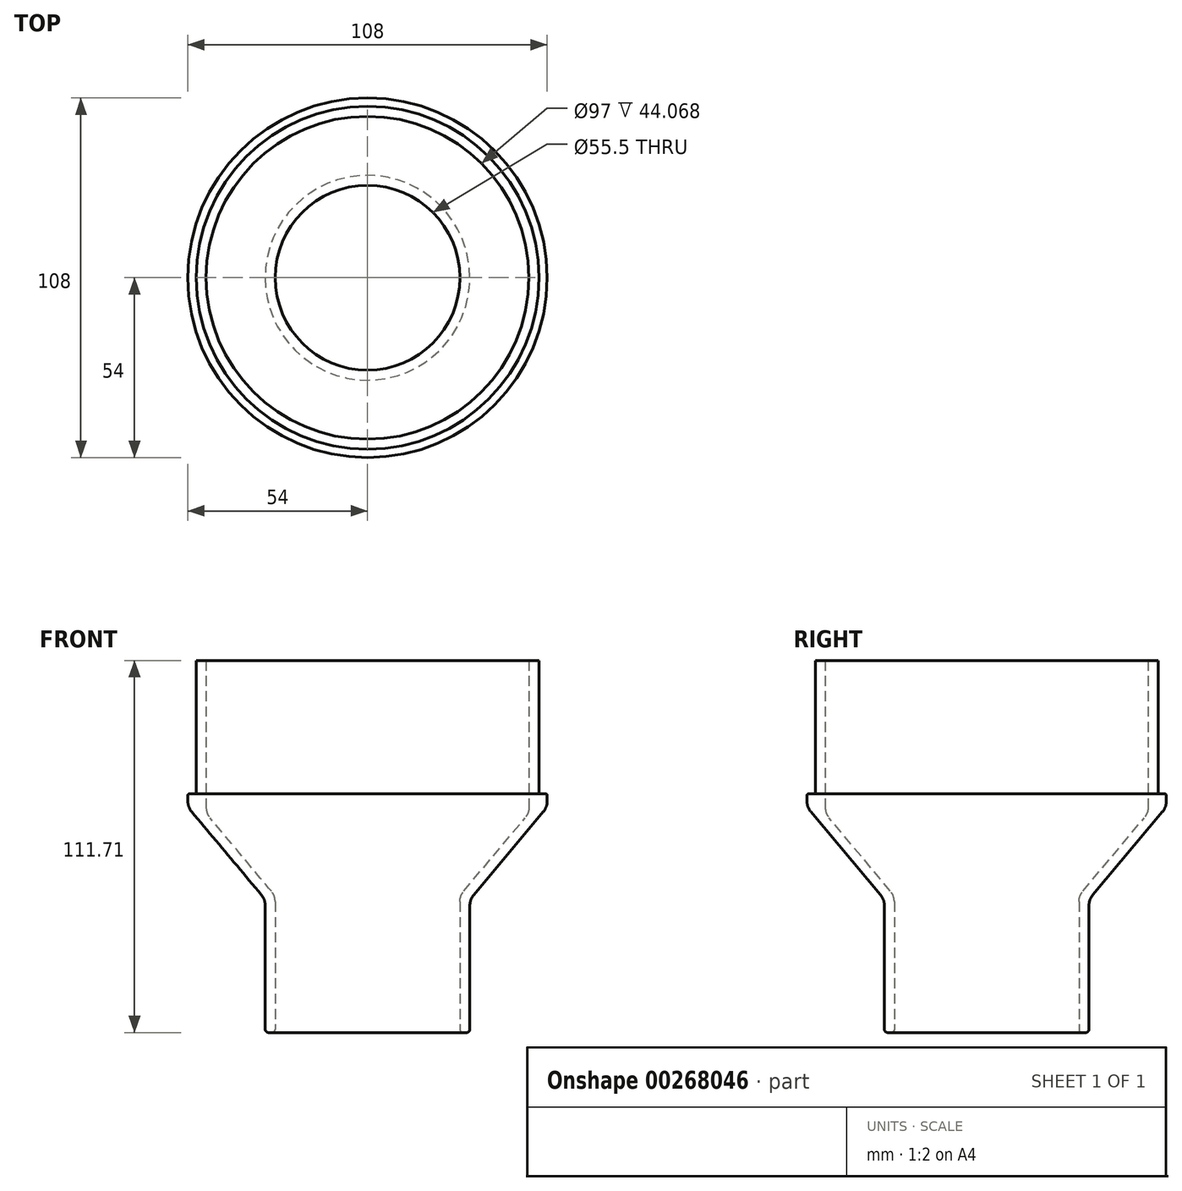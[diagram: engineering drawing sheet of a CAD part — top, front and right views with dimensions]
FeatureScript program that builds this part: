
annotation { "Feature Type Name" : "Feature", "Feature Type Description" : "" }
export const myFeature = defineFeature(function(context is Context, id is Id, definition is map)
    precondition{}
    {
        {
            var Q0;
            Q0=qCreatedBy(makeId("Front.planeOp"),FACE);
            var sketch = newSketch(context, id + "F0", { "sketchPlane" : qUnion([Q0])});
            skLineSegment(sketch, "E0", {"start": v(30.75, 0) * mm, "end": v(30.75, 38.18) * mm});
            skLineSegment(sketch, "E1", {"start": v(31.92, 41.4) * mm, "end": v(52.83, 66.31) * mm});
            skLineSegment(sketch, "E2", {"start": v(54, 69.53) * mm, "end": v(54, 71.7) * mm});
            skLineSegment(sketch, "E3", {"start": v(54, 71.7) * mm, "end": v(51.5, 71.7) * mm});
            skLineSegment(sketch, "E4", {"start": v(51.5, 71.7) * mm, "end": v(51.5, 111.7) * mm});
            skLineSegment(sketch, "E5", {"start": v(0, -37.25) * mm, "end": v(0, 130.62) * mm, "construction": true});
            skLineSegment(sketch, "E6", {"start": v(51.5, 111.7) * mm, "end": v(48.5, 111.7) * mm});
            skLineSegment(sketch, "E7", {"start": v(48.5, 111.7) * mm, "end": v(48.5, 67.64) * mm});
            skLineSegment(sketch, "E8", {"start": v(47.33, 64.43) * mm, "end": v(28.92, 42.49) * mm});
            skLineSegment(sketch, "E9", {"start": v(27.75, 39.27) * mm, "end": v(27.75, 0) * mm});
            skLineSegment(sketch, "E10", {"start": v(27.75, 0) * mm, "end": v(30.75, 0) * mm});
            skPoint(sketch, "E11.visualSharp", {"position": v(48.5, 65.82) * mm});
            skPoint(sketch, "E12.visualSharp", {"position": v(30.75, 40) * mm});
            skPoint(sketch, "E13.visualSharp", {"position": v(27.75, 41.1) * mm});
            skPoint(sketch, "E14.visualSharp", {"position": v(54, 67.7) * mm});
            skLineSegment(sketch, "E15", {"start": v(47.33, 64.43) * mm, "end": v(47.33, 64.43) * mm});
            skLineSegment(sketch, "E16", {"start": v(48.5, 67.64) * mm, "end": v(48.5, 67.64) * mm});
            skLineSegment(sketch, "E17", {"start": v(52.83, 66.31) * mm, "end": v(52.83, 66.31) * mm});
            skLineSegment(sketch, "E18", {"start": v(54, 69.53) * mm, "end": v(54, 69.53) * mm});
            skLineSegment(sketch, "E19", {"start": v(28.92, 42.49) * mm, "end": v(28.92, 42.49) * mm});
            skLineSegment(sketch, "E20", {"start": v(27.75, 39.27) * mm, "end": v(27.75, 39.27) * mm});
            skLineSegment(sketch, "E21", {"start": v(31.92, 41.4) * mm, "end": v(31.92, 41.4) * mm});
            skLineSegment(sketch, "E22", {"start": v(30.75, 38.18) * mm, "end": v(30.75, 38.18) * mm});
            skArc(sketch, "E23.filletArc", {"start": v(47.33, 64.43) * mm, "mid": v(48.2, 65.93) * mm, "end": v(48.5, 67.64) * mm});
            skArc(sketch, "E24.filletArc", {"start": v(52.83, 66.31) * mm, "mid": v(53.7, 67.82) * mm, "end": v(54, 69.53) * mm});
            skArc(sketch, "E25.filletArc", {"start": v(28.92, 42.49) * mm, "mid": v(28.05, 40.98) * mm, "end": v(27.75, 39.27) * mm});
            skArc(sketch, "E26.filletArc", {"start": v(31.92, 41.4) * mm, "mid": v(31.05, 39.9) * mm, "end": v(30.75, 38.18) * mm});
            skSolve(sketch);
        }
        {
            var Q0;
            Q0=makeQuery(id+"F0.imprint","IMPRINT",FACE,{"disambiguationData":[TD([[makeQuery(id+"F0.imprint","IMPRINT",EDGE,{"derivedFrom":sQuery(id+"F0.wireOp",EDGE,"E0")}),1.0]])]});
            var Q1;
            Q1=sQuery(id+"F0.wireOp",EDGE,"E5");
            revolve(context, id + "F1", {"entities" : qUnion([Q0]), "axis" : qUnion([Q1]), "revolveType" : RevolveType.FULL});
        }
        {
            var Q0;
            Q0=makeQuery(id+"F1.opRevolve","SWEPT_EDGE",EDGE,{"disambiguationData":[OSD([sQuery(id+"F0.wireOp",EDGE,"E2"),sQuery(id+"F0.wireOp",EDGE,"E3")])]});
            var Q1;
            Q1=makeQuery(id+"F1.opRevolve","SWEPT_EDGE",EDGE,{"disambiguationData":[OSD([sQuery(id+"F0.wireOp",EDGE,"E3"),sQuery(id+"F0.wireOp",EDGE,"E4")])]});
            fillet(context, id + "F2", {"entities" : qUnion([Q0, Q1]), "radius" : 0.5 * mm, "tangentPropagation" : true, "defaultsChanged" : false, "vertexSettings" : [], "allowEdgeOverflow" : false});
        }
        {
            var Q0;
            Q0=makeQuery(id+"F1.opRevolve","SWEPT_EDGE",EDGE,{"disambiguationData":[OSD([sQuery(id+"F0.wireOp",EDGE,"E17"),sQuery(id+"F0.wireOp",EDGE,"E18")])]});
            var Q1;
            Q1=makeQuery(id+"F1.opRevolve","SWEPT_EDGE",EDGE,{"disambiguationData":[OSD([sQuery(id+"F0.wireOp",EDGE,"E0"),sQuery(id+"F0.wireOp",EDGE,"E10")])]});
            var Q2;
            Q2=makeQuery(id+"F1.opRevolve","SWEPT_EDGE",EDGE,{"disambiguationData":[OSD([sQuery(id+"F0.wireOp",EDGE,"E9"),sQuery(id+"F0.wireOp",EDGE,"E10")])]});
            fillet(context, id + "F3", {"entities" : qUnion([Q0, Q1, Q2]), "tangentPropagation" : true, "radius" : 1 * mm, "defaultsChanged" : false, "vertexSettings" : [], "allowEdgeOverflow" : false});
        }
    });
